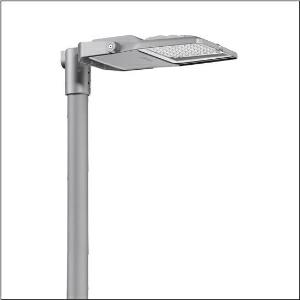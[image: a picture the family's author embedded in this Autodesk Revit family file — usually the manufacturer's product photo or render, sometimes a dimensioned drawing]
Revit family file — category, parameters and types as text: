
# Revit family: floodlight_fl_21_iq_mini___pl64_5xa7772d2e3a_5308
name_source: partatom
category: Lighting Fixtures
units: mm (PartAtom-declared; Revit-internal decimal feet)

## family parameters
Cut with Voids When Loaded = No
Host = Face
Light Source = No
Part Type = Normal
Room Calculation Point = No
Round Connector Dimension = Use Diameter
Shared = No

## types (1)
- --- (1 x LED, 17220 lm, 143 W, 3000K)
    Apparent Load = 143 VA
    CIE Flux Codes = 28 80 98 100 100
    Color Rendering = 70
    Color Temperature = 3000K
    Default Elevation = 1800 mm
    Description = Floodlight FL 21 iQ mini, floodlight, primary light control with lens, of PMMA, primary optical cover: protective disc, of toughened safety glass, transparent, light distribution: PL64, light emission: direct distribution, installation type: surface-mounted, LED, High Power LED, rated luminous flux: 17.220lm, luminous efficacy: 120lm/W, light colour: 730, colour temperature: 3000K, control: Auto-Match, Temp-Guard, Night-Set, Smart-Wire, Desk-Remote (wireless, voltage-free reading and setting of iQ features in the workshop via application-optimized NFC function/RFID function), optimised constant luminous flux control (CLO 2.0), Light-Fading, Lumen-Switch, with terminal, 6-pole, mains connection: 220..240V, AC, 50/60Hz, start of lifetime: 143W, end of service life: 152W, reduction: 61W, luminaire housing, of diecast aluminium, powder-coated, Siteco® metallic grey (DB 702S), corrosivity category C5 mid according to DIN EN ISO 12944, sealing non-destructively replaceable, please order mast flange separately, mast bracket, of steel, galvanised, powder-coated, protection rating (complete): IP66, insulation class (complete): insulation class II (safety insulation), certification: CE, ENEC, VDE, protection symbol: D, impact resistance: IK08, permissible operating ambient temperature: -40..+40°C, permissible operating ambient temperature for outdoor applications: -40..+50°C, standard: DIN EN 12944, LABS conformity tested according to VDMA 24364:2018-05, packaging unit: 1 piece

Light Distribution: PL64
    Height = 70 mm
    Lamp = 1 x LED
    Lamp Light Flux = 17220 lm
    Lamp Power = 143 W
    Lamp count = 1
    Length = 485 mm
    Luminous efficacy = 120 lm/W
    Manufacturer = Siteco
    ModVariant = No
    Model = 5XA7772D2E3A
    Number of Poles = 1
    OnlyDefault = Yes
    Power Factor = 1
    Product Name = Floodlight FL 21 iQ mini | PL64
    Product group = floodlight | pylon annexe
    ProductGroupID = 6200
    Protection Class = Protection class II
    Protection Degree = IP 66
    RLX_Detail_Level = 1
    RLX_Emergency_Light_Flux = 0 lm
    RLX_Emergency_Type = 0
    RLX_Emergency_Type_DB = No
    RlxData = <blob elided: 101581 chars, md5=d52d743e>
    Socket = socket
    Standby Power = 0 W
    System Light Flux = 17220 lm
    System Power = 143 W
    Type Comments = factory setting: luminous flux: 100 % | dim-lin: 254 | 730 mA
    Type Image = l_1007125.jpg
    URL = http://relux.com
    VarID = @adj_098101
    Voltage = 0 V
    Weight = 0.00 kg
    Width = 337 mm

## geometry (parser evidence)
native form markers: Blend x4, Sweep x11
no freeform markers — native parametric forms only
